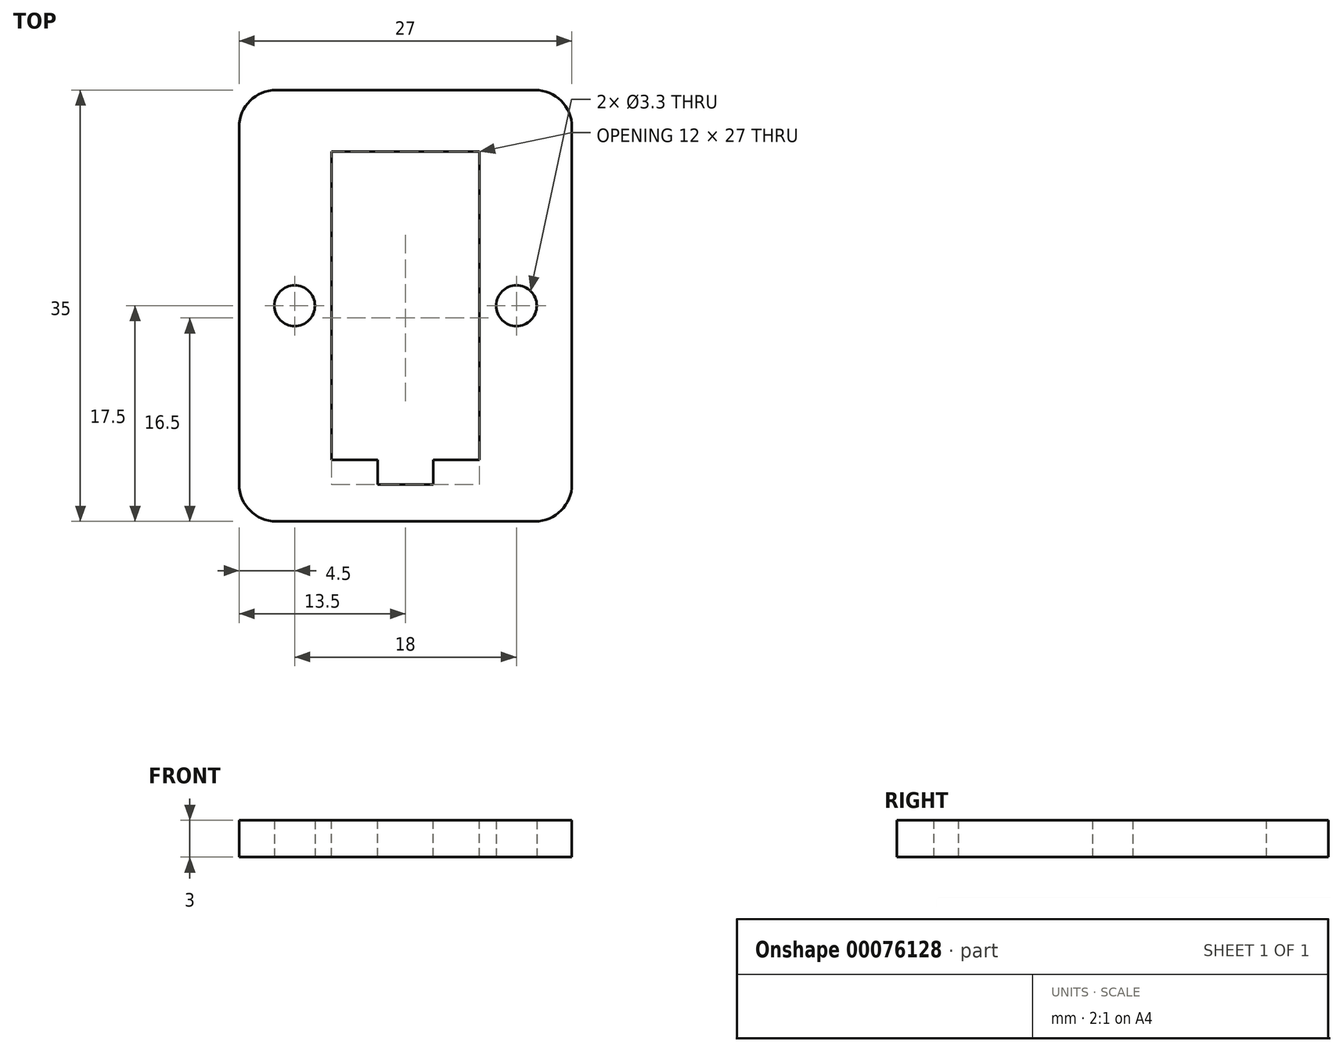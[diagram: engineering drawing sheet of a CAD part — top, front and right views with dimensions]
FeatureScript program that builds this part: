
annotation { "Feature Type Name" : "Feature", "Feature Type Description" : "" }
export const myFeature = defineFeature(function(context is Context, id is Id, definition is map)
    precondition{}
    {
        {
            var Q0;
            Q0=qCreatedBy(makeId("Top.planeOp"),FACE);
            var sketch = newSketch(context, id + "F0", { "sketchPlane" : qUnion([Q0])});
            skLineSegment(sketch, "E0.bottom", {"start": v(-10.5, 17.5) * mm, "end": v(10.5, 17.5) * mm});
            skLineSegment(sketch, "E0.top", {"start": v(-10.5, -17.5) * mm, "end": v(10.5, -17.5) * mm});
            skLineSegment(sketch, "E0.left", {"start": v(-13.5, 14.5) * mm, "end": v(-13.5, -14.5) * mm});
            skLineSegment(sketch, "E0.right", {"start": v(13.5, 14.5) * mm, "end": v(13.5, -14.5) * mm});
            skPoint(sketch, "E0.middle", {"position": v(0, 0) * mm});
            skPoint(sketch, "E1.visualSharp", {"position": v(-13.5, 17.5) * mm});
            skArc(sketch, "E1.filletArc", {"start": v(-10.5, 17.5) * mm, "mid": v(-12.62, 16.62) * mm, "end": v(-13.5, 14.5) * mm});
            skPoint(sketch, "E2.visualSharp", {"position": v(13.5, 17.5) * mm});
            skArc(sketch, "E2.filletArc", {"start": v(13.5, 14.5) * mm, "mid": v(12.62, 16.62) * mm, "end": v(10.5, 17.5) * mm});
            skPoint(sketch, "E3.visualSharp", {"position": v(13.5, -17.5) * mm});
            skArc(sketch, "E3.filletArc", {"start": v(10.5, -17.5) * mm, "mid": v(12.62, -16.62) * mm, "end": v(13.5, -14.5) * mm});
            skPoint(sketch, "E4.visualSharp", {"position": v(-13.5, -17.5) * mm});
            skArc(sketch, "E4.filletArc", {"start": v(-13.5, -14.5) * mm, "mid": v(-12.62, -16.62) * mm, "end": v(-10.5, -17.5) * mm});
            skSolve(sketch);
        }
        {
            var Q0;
            Q0 = qSketchRegion(id + "F0", true);
            extrude(context, id + "F1", {"entities" : qUnion([Q0]), "depth" : 3 * mm});
        }
        {
            var Q0;
            Q0=makeQuery(id+"F1.opExtrude","CAP_FACE",FACE,{"disambiguationData":[OSD([sQuery(id+"F0.wireOp",EDGE,"E0.bottom"),sQuery(id+"F0.wireOp",EDGE,"E0.top"),sQuery(id+"F0.wireOp",EDGE,"E0.left"),sQuery(id+"F0.wireOp",EDGE,"E0.right"),sQuery(id+"F0.wireOp",EDGE,"E1.filletArc"),sQuery(id+"F0.wireOp",EDGE,"E2.filletArc"),sQuery(id+"F0.wireOp",EDGE,"E3.filletArc"),sQuery(id+"F0.wireOp",EDGE,"E4.filletArc")])],"isStart":false});
            var sketch = newSketch(context, id + "F2", { "sketchPlane" : qUnion([Q0])});
            skCircle(sketch, "E5", {"center": v(-9, 0) * mm, "radius": 1.65 * mm});
            skCircle(sketch, "E6", {"center": v(9, 0) * mm, "radius": 1.65 * mm});
            skSolve(sketch);
        }
        {
            var Q0;
            Q0=sQuery(id+"F2.wireOp",VERTEX,"E5.center");
            var Q1;
            Q1=sQuery(id+"F2.wireOp",VERTEX,"E6.center");
            var Q2;
            Q2=makeQuery(id+"F1.opExtrude","SWEPT_BODY",BODY,{"disambiguationData":[OSD([sQuery(id+"F0.wireOp",EDGE,"E0.bottom"),sQuery(id+"F0.wireOp",EDGE,"E0.top"),sQuery(id+"F0.wireOp",EDGE,"E0.left"),sQuery(id+"F0.wireOp",EDGE,"E0.right"),sQuery(id+"F0.wireOp",EDGE,"E1.filletArc"),sQuery(id+"F0.wireOp",EDGE,"E2.filletArc"),sQuery(id+"F0.wireOp",EDGE,"E3.filletArc"),sQuery(id+"F0.wireOp",EDGE,"E4.filletArc")])]});
            hole(context, id + "F3", {"style" : HoleStyle.SIMPLE, "endStyle" : HoleEndStyle.THROUGH, "holeDiameter" : 3.3 * mm, "locations" : qUnion([Q0, Q1]), "scope" : qUnion([Q2]), "isTappedThrough" : true, "startStyle" : HoleStartStyle.PART});
        }
        {
            var Q0;
            Q0=makeQuery(id+"F1.opExtrude","CAP_FACE",FACE,{"disambiguationData":[OSD([sQuery(id+"F0.wireOp",EDGE,"E0.bottom"),sQuery(id+"F0.wireOp",EDGE,"E0.top"),sQuery(id+"F0.wireOp",EDGE,"E0.left"),sQuery(id+"F0.wireOp",EDGE,"E0.right"),sQuery(id+"F0.wireOp",EDGE,"E1.filletArc"),sQuery(id+"F0.wireOp",EDGE,"E2.filletArc"),sQuery(id+"F0.wireOp",EDGE,"E3.filletArc"),sQuery(id+"F0.wireOp",EDGE,"E4.filletArc")])],"isStart":false});
            var sketch = newSketch(context, id + "F4", { "sketchPlane" : qUnion([Q0])});
            skLineSegment(sketch, "E7.bottom", {"start": v(-6, 12.5) * mm, "end": v(6, 12.5) * mm});
            skLineSegment(sketch, "E7.top", {"start": v(-6, -12.5) * mm, "end": v(-2.25, -12.5) * mm});
            skLineSegment(sketch, "E7.left", {"start": v(-6, 12.5) * mm, "end": v(-6, -12.5) * mm});
            skLineSegment(sketch, "E7.right", {"start": v(6, 12.5) * mm, "end": v(6, -12.5) * mm});
            skPoint(sketch, "E7.middle", {"position": v(0, 0) * mm});
            skLineSegment(sketch, "E8.bottom", {"start": v(-2.25, -14.5) * mm, "end": v(2.25, -14.5) * mm});
            skLineSegment(sketch, "E8.left", {"start": v(-2.25, -14.5) * mm, "end": v(-2.25, -12.5) * mm});
            skLineSegment(sketch, "E8.right", {"start": v(2.25, -14.5) * mm, "end": v(2.25, -12.5) * mm});
            skLineSegment(sketch, "E9.trimOffspring", {"start": v(2.25, -12.5) * mm, "end": v(6, -12.5) * mm});
            skSolve(sketch);
        }
        {
            var Q0;
            Q0 = qSketchRegion(id + "F4", true);
            extrude(context, id + "F5", {"entities" : qUnion([Q0]), "operationType" : NewBodyOperationType.REMOVE, "endBound" : BoundingType.THROUGH_ALL, "oppositeDirection" : true, "depth" : 25 * mm});
        }
    });
